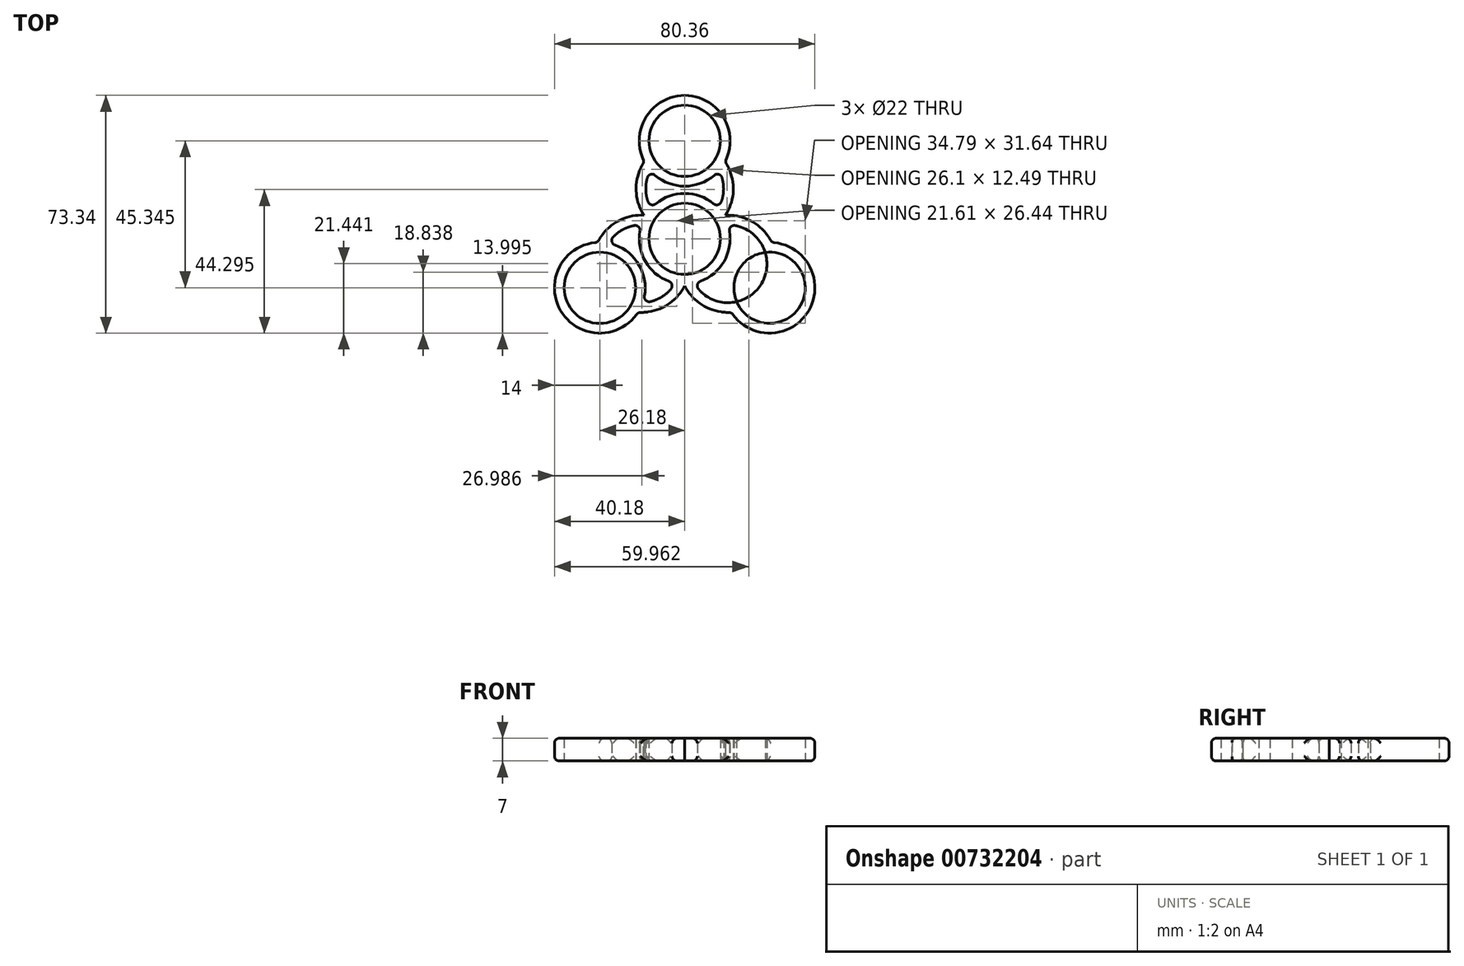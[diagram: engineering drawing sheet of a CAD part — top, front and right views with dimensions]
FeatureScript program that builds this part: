
annotation { "Feature Type Name" : "Feature", "Feature Type Description" : "" }
export const myFeature = defineFeature(function(context is Context, id is Id, definition is map)
    precondition{}
    {
        {
            var Q0;
            Q0=qCreatedBy(makeId("Top.planeOp"),FACE);
            var sketch = newSketch(context, id + "F0", { "sketchPlane" : qUnion([Q0])});
            skCircle(sketch, "E0", {"center": v(0, 0) * mm, "radius": 11 * mm});
            skCircle(sketch, "E1", {"center": v(0, 0) * mm, "radius": 14 * mm});
            skCircle(sketch, "E2", {"center": v(0, 30.23) * mm, "radius": 11 * mm});
            skCircle(sketch, "E3", {"center": v(0, 30.23) * mm, "radius": 14 * mm});
            skCircle(sketch, "E4", {"center": v(0, 15.44) * mm, "radius": 12 * mm});
            skCircle(sketch, "E5", {"center": v(0, 15.44) * mm, "radius": 15 * mm});
            skCircle(sketch, "E6.1.0", {"center": v(-13.37, -7.72) * mm, "radius": 12 * mm});
            skCircle(sketch, "E6.1.1", {"center": v(-13.37, -7.72) * mm, "radius": 15 * mm});
            skCircle(sketch, "E6.1.2", {"center": v(-26.18, -15.11) * mm, "radius": 14 * mm});
            skCircle(sketch, "E6.1.3", {"center": v(-26.18, -15.11) * mm, "radius": 11 * mm});
            skCircle(sketch, "E6.2.0", {"center": v(13.37, -7.72) * mm, "radius": 12 * mm});
            skCircle(sketch, "E6.2.1", {"center": v(13.37, -7.72) * mm, "radius": 15 * mm});
            skCircle(sketch, "E6.2.2", {"center": v(26.18, -15.11) * mm, "radius": 14 * mm});
            skCircle(sketch, "E6.2.3", {"center": v(26.18, -15.11) * mm, "radius": 11 * mm});
            skSolve(sketch);
        }
        {
            var Q0;
            Q0=qSketchRegion(id+"F0",true);
            var Q1;
            {var subQ0=sQuery(id+"F0.wireOp",EDGE,"E4");var subQ1=sQuery(id+"F0.wireOp",EDGE,"E2");var subQ2=makeQuery(id+"F0.imprint","INTERSECT",VERTEX,{"disambiguationData":[OD(0.0)],"derivedFrom":[subQ1,subQ0]});Q1=makeQuery(id+"F0.imprint","IMPRINT",FACE,{"disambiguationData":[TD([[makeQuery(id+"F0.imprint","IMPRINT",EDGE,{"disambiguationData":[TD([[subQ2,-1.0]])],"derivedFrom":subQ1}),-1.0]])]});}
            var Q2;
            {var subQ0=sQuery(id+"F0.wireOp",EDGE,"E4");var subQ1=sQuery(id+"F0.wireOp",EDGE,"E0");var subQ2=makeQuery(id+"F0.imprint","INTERSECT",VERTEX,{"disambiguationData":[OD(0.0)],"derivedFrom":[subQ1,subQ0]});Q2=makeQuery(id+"F0.imprint","IMPRINT",FACE,{"disambiguationData":[TD([[makeQuery(id+"F0.imprint","IMPRINT",EDGE,{"disambiguationData":[TD([[subQ2,-1.0]])],"derivedFrom":subQ1}),-1.0]])]});}
            var Q3;
            {var subQ0=sQuery(id+"F0.wireOp",EDGE,"E5");var subQ1=sQuery(id+"F0.wireOp",EDGE,"E0");var subQ2=makeQuery(id+"F0.imprint","INTERSECT",VERTEX,{"disambiguationData":[OD(0.0)],"derivedFrom":[subQ1,subQ0]});Q3=makeQuery(id+"F0.imprint","IMPRINT",FACE,{"disambiguationData":[TD([[makeQuery(id+"F0.imprint","IMPRINT",EDGE,{"disambiguationData":[TD([[subQ2,1.0]])],"derivedFrom":subQ1}),-1.0]])]});}
            var Q4;
            {var subQ0=sQuery(id+"F0.wireOp",EDGE,"E5");var subQ1=sQuery(id+"F0.wireOp",EDGE,"E0");var subQ2=makeQuery(id+"F0.imprint","INTERSECT",VERTEX,{"disambiguationData":[OD(0.0)],"derivedFrom":[subQ1,subQ0]});Q4=makeQuery(id+"F0.imprint","IMPRINT",FACE,{"disambiguationData":[TD([[makeQuery(id+"F0.imprint","IMPRINT",EDGE,{"disambiguationData":[TD([[subQ2,-1.0]])],"derivedFrom":subQ1}),-1.0]])]});}
            var Q5;
            {var subQ0=sQuery(id+"F0.wireOp",EDGE,"E6.2.1");var subQ1=sQuery(id+"F0.wireOp",EDGE,"E0");var subQ2=makeQuery(id+"F0.imprint","INTERSECT",VERTEX,{"disambiguationData":[OD(0.0)],"derivedFrom":[subQ1,subQ0]});Q5=makeQuery(id+"F0.imprint","IMPRINT",FACE,{"disambiguationData":[TD([[makeQuery(id+"F0.imprint","IMPRINT",EDGE,{"disambiguationData":[TD([[subQ2,-1.0]])],"derivedFrom":subQ1}),-1.0]])]});}
            var Q6;
            {var subQ0=sQuery(id+"F0.wireOp",EDGE,"E6.2.0");var subQ1=sQuery(id+"F0.wireOp",EDGE,"E0");var subQ2=makeQuery(id+"F0.imprint","INTERSECT",VERTEX,{"disambiguationData":[OD(0.0)],"derivedFrom":[subQ1,subQ0]});Q6=makeQuery(id+"F0.imprint","IMPRINT",FACE,{"disambiguationData":[TD([[makeQuery(id+"F0.imprint","IMPRINT",EDGE,{"disambiguationData":[TD([[subQ2,1.0]])],"derivedFrom":subQ1}),-1.0]])]});}
            var Q7;
            {var subQ0=sQuery(id+"F0.wireOp",EDGE,"E4");var subQ1=sQuery(id+"F0.wireOp",EDGE,"E0");var subQ2=makeQuery(id+"F0.imprint","INTERSECT",VERTEX,{"disambiguationData":[OD(1.0)],"derivedFrom":[subQ1,subQ0]});Q7=makeQuery(id+"F0.imprint","IMPRINT",FACE,{"disambiguationData":[TD([[makeQuery(id+"F0.imprint","IMPRINT",EDGE,{"disambiguationData":[TD([[subQ2,-1.0]])],"derivedFrom":subQ1}),-1.0]])]});}
            var Q8;
            {var subQ0=sQuery(id+"F0.wireOp",EDGE,"E5");var subQ1=sQuery(id+"F0.wireOp",EDGE,"E0");var subQ2=makeQuery(id+"F0.imprint","INTERSECT",VERTEX,{"disambiguationData":[OD(1.0)],"derivedFrom":[subQ1,subQ0]});Q8=makeQuery(id+"F0.imprint","IMPRINT",FACE,{"disambiguationData":[TD([[makeQuery(id+"F0.imprint","IMPRINT",EDGE,{"disambiguationData":[TD([[subQ2,-1.0]])],"derivedFrom":subQ1}),-1.0]])]});}
            var Q9;
            {var subQ0=sQuery(id+"F0.wireOp",EDGE,"E6.1.1");var subQ1=sQuery(id+"F0.wireOp",EDGE,"E0");var subQ2=makeQuery(id+"F0.imprint","INTERSECT",VERTEX,{"disambiguationData":[OD(0.0)],"derivedFrom":[subQ1,subQ0]});Q9=makeQuery(id+"F0.imprint","IMPRINT",FACE,{"disambiguationData":[TD([[makeQuery(id+"F0.imprint","IMPRINT",EDGE,{"disambiguationData":[TD([[subQ2,-1.0]])],"derivedFrom":subQ1}),-1.0]])]});}
            var Q10;
            {var subQ0=sQuery(id+"F0.wireOp",EDGE,"E6.1.0");var subQ1=sQuery(id+"F0.wireOp",EDGE,"E0");var subQ2=makeQuery(id+"F0.imprint","INTERSECT",VERTEX,{"disambiguationData":[OD(0.0)],"derivedFrom":[subQ1,subQ0]});Q10=makeQuery(id+"F0.imprint","IMPRINT",FACE,{"disambiguationData":[TD([[makeQuery(id+"F0.imprint","IMPRINT",EDGE,{"disambiguationData":[TD([[subQ2,-1.0]])],"derivedFrom":subQ1}),-1.0]])]});}
            var Q11;
            {var subQ0=sQuery(id+"F0.wireOp",EDGE,"E6.1.0");var subQ1=sQuery(id+"F0.wireOp",EDGE,"E0");var subQ2=makeQuery(id+"F0.imprint","INTERSECT",VERTEX,{"disambiguationData":[OD(1.0)],"derivedFrom":[subQ1,subQ0]});Q11=makeQuery(id+"F0.imprint","IMPRINT",FACE,{"disambiguationData":[TD([[makeQuery(id+"F0.imprint","IMPRINT",EDGE,{"disambiguationData":[TD([[subQ2,-1.0]])],"derivedFrom":subQ1}),-1.0]])]});}
            var Q12;
            {var subQ0=sQuery(id+"F0.wireOp",EDGE,"E6.1.1");var subQ1=sQuery(id+"F0.wireOp",EDGE,"E0");var subQ2=makeQuery(id+"F0.imprint","INTERSECT",VERTEX,{"disambiguationData":[OD(1.0)],"derivedFrom":[subQ1,subQ0]});Q12=makeQuery(id+"F0.imprint","IMPRINT",FACE,{"disambiguationData":[TD([[makeQuery(id+"F0.imprint","IMPRINT",EDGE,{"disambiguationData":[TD([[subQ2,-1.0]])],"derivedFrom":subQ1}),-1.0]])]});}
            var Q13;
            {var subQ0=sQuery(id+"F0.wireOp",EDGE,"E6.2.1");var subQ1=sQuery(id+"F0.wireOp",EDGE,"E0");var subQ2=makeQuery(id+"F0.imprint","INTERSECT",VERTEX,{"disambiguationData":[OD(1.0)],"derivedFrom":[subQ1,subQ0]});Q13=makeQuery(id+"F0.imprint","IMPRINT",FACE,{"disambiguationData":[TD([[makeQuery(id+"F0.imprint","IMPRINT",EDGE,{"disambiguationData":[TD([[subQ2,-1.0]])],"derivedFrom":subQ1}),-1.0]])]});}
            var Q14;
            {var subQ0=sQuery(id+"F0.wireOp",EDGE,"E6.2.3");var subQ1=sQuery(id+"F0.wireOp",EDGE,"E6.2.0");var subQ2=makeQuery(id+"F0.imprint","INTERSECT",VERTEX,{"disambiguationData":[OD(0.0)],"derivedFrom":[subQ1,subQ0]});Q14=makeQuery(id+"F0.imprint","IMPRINT",FACE,{"disambiguationData":[TD([[makeQuery(id+"F0.imprint","IMPRINT",EDGE,{"disambiguationData":[TD([[subQ2,1.0]])],"derivedFrom":subQ1}),1.0]])]});}
            var Q15;
            {var subQ0=sQuery(id+"F0.wireOp",EDGE,"E6.1.3");var subQ1=sQuery(id+"F0.wireOp",EDGE,"E6.1.0");var subQ2=makeQuery(id+"F0.imprint","INTERSECT",VERTEX,{"disambiguationData":[OD(0.0)],"derivedFrom":[subQ1,subQ0]});Q15=makeQuery(id+"F0.imprint","IMPRINT",FACE,{"disambiguationData":[TD([[makeQuery(id+"F0.imprint","IMPRINT",EDGE,{"disambiguationData":[TD([[subQ2,1.0]])],"derivedFrom":subQ1}),1.0]])]});}
            extrude(context, id + "F1", {"entities" : qUnion([Q0, Q1, Q2, Q3, Q4, Q5, Q6, Q7, Q8, Q9, Q10, Q11, Q12, Q13, Q14, Q15]), "depth" : 7 * mm, "offsetDistance" : 25 * mm});
        }
        {
            var Q0;
            {var subQ0=sQuery(id+"F0.wireOp",EDGE,"E5");var subQ1=sQuery(id+"F0.wireOp",EDGE,"E3");Q0=makeQuery(id+"F1.opExtrude","SWEPT_FACE",FACE,{"disambiguationData":[OSD([subQ1]),TDD([makeQuery(id+"F0.imprint","IMPRINT",EDGE,{"disambiguationData":[TD([[makeQuery(id+"F0.imprint","INTERSECT",VERTEX,{"disambiguationData":[OD(0.0)],"derivedFrom":[subQ1,subQ0]}),1.0]])],"derivedFrom":subQ1})])]});}
            var Q1;
            {var subQ0=sQuery(id+"F0.wireOp",EDGE,"E6.1.2");var subQ1=sQuery(id+"F0.wireOp",EDGE,"E6.1.1");Q1=makeQuery(id+"F1.opExtrude","SWEPT_FACE",FACE,{"disambiguationData":[OSD([subQ0]),TDD([makeQuery(id+"F0.imprint","IMPRINT",EDGE,{"disambiguationData":[TD([[makeQuery(id+"F0.imprint","INTERSECT",VERTEX,{"disambiguationData":[OD(0.0)],"derivedFrom":[subQ1,subQ0]}),-1.0]])],"derivedFrom":subQ0})])]});}
            var Q2;
            {var subQ0=sQuery(id+"F0.wireOp",EDGE,"E6.2.2");var subQ1=sQuery(id+"F0.wireOp",EDGE,"E6.2.1");Q2=makeQuery(id+"F1.opExtrude","SWEPT_FACE",FACE,{"disambiguationData":[OSD([subQ0]),TDD([makeQuery(id+"F0.imprint","IMPRINT",EDGE,{"disambiguationData":[TD([[makeQuery(id+"F0.imprint","INTERSECT",VERTEX,{"disambiguationData":[OD(0.0)],"derivedFrom":[subQ1,subQ0]}),-1.0]])],"derivedFrom":subQ0})])]});}
            var Q3;
            {var subQ0=sQuery(id+"F0.wireOp",EDGE,"E6.2.0");var subQ1=sQuery(id+"F0.wireOp",EDGE,"E1");Q3=makeQuery(id+"F1.opExtrude","SWEPT_FACE",FACE,{"disambiguationData":[OSD([subQ1]),TDD([makeQuery(id+"F0.imprint","IMPRINT",EDGE,{"disambiguationData":[TD([[makeQuery(id+"F0.imprint","INTERSECT",VERTEX,{"disambiguationData":[OD(0.0)],"derivedFrom":[subQ1,subQ0]}),1.0]])],"derivedFrom":subQ1})])]});}
            var Q4;
            {var subQ0=sQuery(id+"F0.wireOp",EDGE,"E4");var subQ1=sQuery(id+"F0.wireOp",EDGE,"E3");Q4=makeQuery(id+"F1.opExtrude","SWEPT_FACE",FACE,{"disambiguationData":[OSD([subQ1]),TDD([makeQuery(id+"F0.imprint","IMPRINT",EDGE,{"disambiguationData":[TD([[makeQuery(id+"F0.imprint","INTERSECT",VERTEX,{"disambiguationData":[OD(0.0)],"derivedFrom":[subQ1,subQ0]}),-1.0]])],"derivedFrom":subQ1})])]});}
            var Q5;
            {var subQ0=sQuery(id+"F0.wireOp",EDGE,"E6.1.2");var subQ1=sQuery(id+"F0.wireOp",EDGE,"E6.1.0");Q5=makeQuery(id+"F1.opExtrude","SWEPT_FACE",FACE,{"disambiguationData":[OSD([subQ0]),TDD([makeQuery(id+"F0.imprint","IMPRINT",EDGE,{"disambiguationData":[TD([[makeQuery(id+"F0.imprint","INTERSECT",VERTEX,{"disambiguationData":[OD(0.0)],"derivedFrom":[subQ1,subQ0]}),1.0]])],"derivedFrom":subQ0})])]});}
            var Q6;
            {var subQ0=sQuery(id+"F0.wireOp",EDGE,"E6.1.0");var subQ1=sQuery(id+"F0.wireOp",EDGE,"E1");Q6=makeQuery(id+"F1.opExtrude","SWEPT_FACE",FACE,{"disambiguationData":[OSD([subQ1]),TDD([makeQuery(id+"F0.imprint","IMPRINT",EDGE,{"disambiguationData":[TD([[makeQuery(id+"F0.imprint","INTERSECT",VERTEX,{"disambiguationData":[OD(0.0)],"derivedFrom":[subQ1,subQ0]}),-1.0]])],"derivedFrom":subQ1})])]});}
            var Q7;
            {var subQ0=sQuery(id+"F0.wireOp",EDGE,"E4");var subQ1=sQuery(id+"F0.wireOp",EDGE,"E1");Q7=makeQuery(id+"F1.opExtrude","SWEPT_FACE",FACE,{"disambiguationData":[OSD([subQ1]),TDD([makeQuery(id+"F0.imprint","IMPRINT",EDGE,{"disambiguationData":[TD([[makeQuery(id+"F0.imprint","INTERSECT",VERTEX,{"disambiguationData":[OD(0.0)],"derivedFrom":[subQ1,subQ0]}),-1.0]])],"derivedFrom":subQ1})])]});}
            var Q8;
            {var subQ0=sQuery(id+"F0.wireOp",EDGE,"E6.2.2");var subQ1=sQuery(id+"F0.wireOp",EDGE,"E6.2.0");Q8=makeQuery(id+"F1.opExtrude","SWEPT_FACE",FACE,{"disambiguationData":[OSD([subQ0]),TDD([makeQuery(id+"F0.imprint","IMPRINT",EDGE,{"disambiguationData":[TD([[makeQuery(id+"F0.imprint","INTERSECT",VERTEX,{"disambiguationData":[OD(0.0)],"derivedFrom":[subQ1,subQ0]}),1.0]])],"derivedFrom":subQ0})])]});}
            fillet(context, id + "F2", {"entities" : qUnion([Q0, Q1, Q2, Q3, Q4, Q5, Q6, Q7, Q8]), "radius" : 1.5 * mm, "tangentPropagation" : true, "allowEdgeOverflow" : false});
        }
    });
